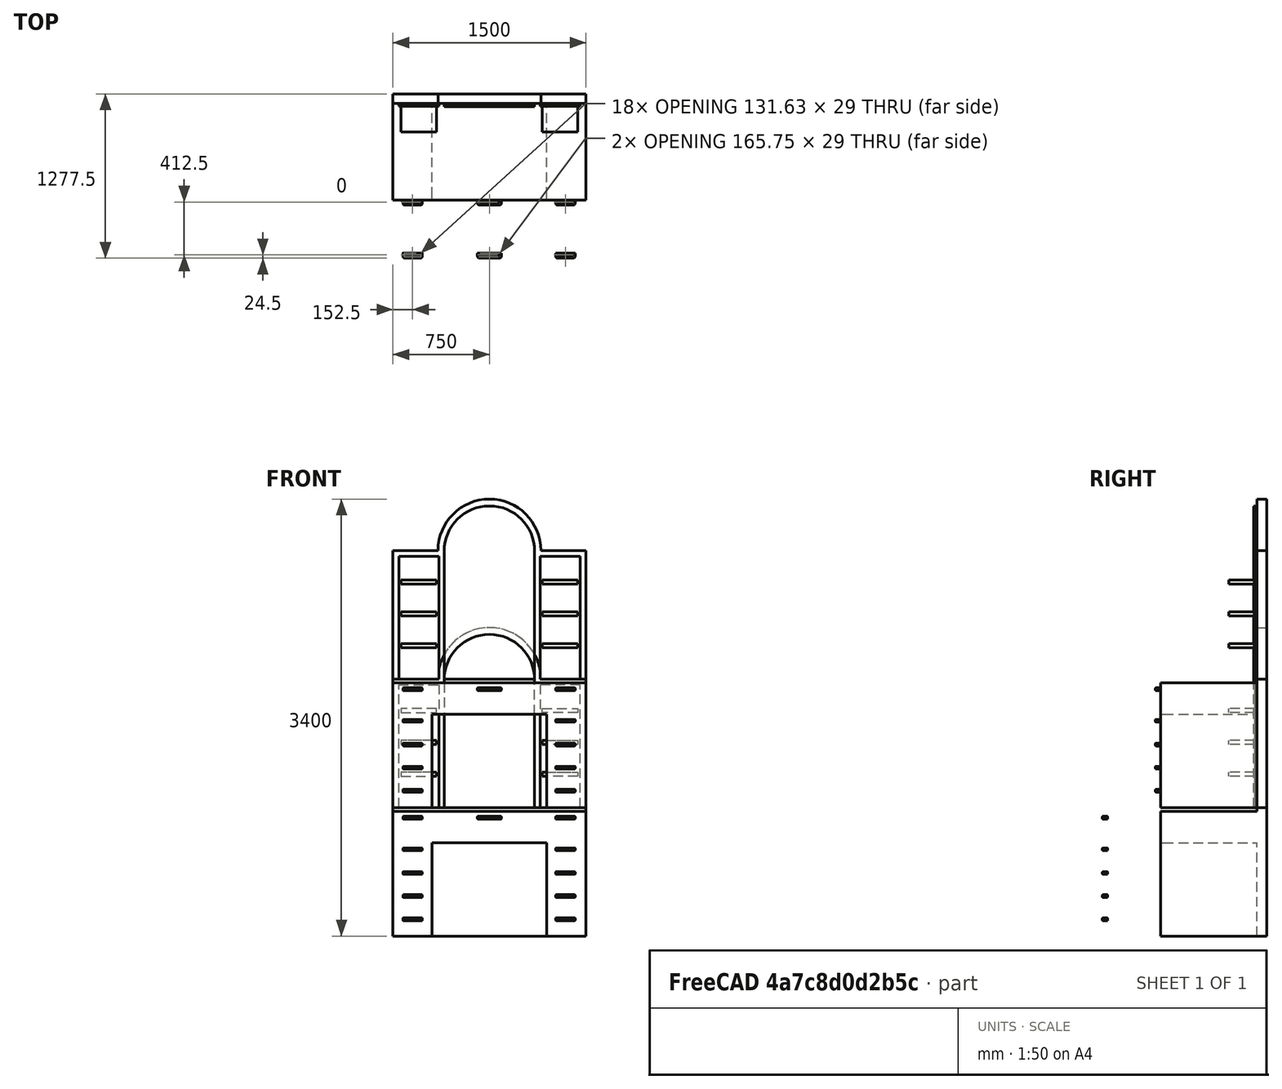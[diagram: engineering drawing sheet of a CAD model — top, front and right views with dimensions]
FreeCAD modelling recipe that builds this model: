
FCSTD DOCUMENT  (FreeCAD 1.0R39109 (Git))
Label: DressingTable
License: All rights reserved
LicenseURL: https://en.wikipedia.org/wiki/All_rights_reserved
objects: Sketcher::SketchObject×30, PartDesign::Fillet×22, PartDesign::Pad×18, PartDesign::Body×13, PartDesign::Pocket×12, PartDesign::ShapeBinder×12, PartDesign::Plane×12, Assembly::JointGroup×3, App::Link×3, Assembly::AssemblyObject×3, Part::FeaturePython×3, App::Part×2
note: 256 computed .brp shape members not serialized (recipe doc carries the construction recipe); baked Part::Feature solids carry a one-line shape summary decoded from their .brp

FEATURE [Sketcher::SketchObject] Sketch
  ArcFitTolerance = 1e-06
  AttachmentSupport = -> [XZ_Plane]
  FullyConstrained = true
  MakeInternals = false
  MapMode = 5
  Placement = pos=(0,0,0) rot=(1,0,0;1.5708rad)
  sketch-geometry (7):
    g0: LineSegment StartX=-750 StartY=-1000 StartZ=0 EndX=750 EndY=-1000 EndZ=0
    g1: LineSegment StartX=750 StartY=-1000 StartZ=0 EndX=750 EndY=1000 EndZ=0
    g2: LineSegment StartX=750 StartY=1000 StartZ=0 EndX=400 EndY=1000 EndZ=0
    g3: LineSegment StartX=-750 StartY=1000 StartZ=0 EndX=-750 EndY=-1000 EndZ=0
    g4: GeomPoint [constr] X=0 Y=0 Z=0
    g5: ArcOfCircle CenterX=1.35e-14 CenterY=1000 CenterZ=0 NormalX=0 NormalY=0 NormalZ=1 AngleXU=0 Radius=400 StartAngle=0 EndAngle=3.14159
    g6: LineSegment StartX=-400 StartY=1000 StartZ=0 EndX=-750 EndY=1000 EndZ=0
  constraints (18):
    c: Coincident(g0,g1)
    c: Coincident(g1,g2)
    c: Coincident(g6,g3)
    c: Coincident(g3,g0)
    c: Horizontal(g0)
    c: Horizontal(g2)
    c: Vertical(g1)
    c: Vertical(g3)
    c: Symmetric(g2,g0,g4)
    c: Coincident(g4,g-1)
    c: DistanceY(g1,g1) = 2000
    c: DistanceX(g6,g2) = 1500
    c: Symmetric(g1,g6,g5)
    c: Diameter(g5) = 800
    c: Coincident(g5,g6)
    c: Coincident(g5,g2)
    c: Horizontal(g6)
    c: Horizontal(g5,g2)
FEATURE [PartDesign::Pad] Pad
  Direction = (0,-1,2e-16)
  Length = 75
  Length2 = 10
  Placement = pos=(0,0,0) rot=(1,0,0;1.5708rad)
  Profile = -> Sketch
  ReferenceAxis = -> Sketch [N_Axis]
  Refine = true
  Suppressed = false
  Type = 0
FEATURE [Sketcher::SketchObject] Sketch001
  ArcFitTolerance = 1e-06
  AttachmentSupport = -> [Pad]
  FullyConstrained = false
  MakeInternals = false
  MapMode = 5
  Placement = pos=(0,-75,0) rot=(1,0,0;1.5708rad)
  sketch-geometry (14):
    g0: LineSegment [constr] StartX=0 StartY=0 StartZ=0 EndX=936.468 EndY=0 EndZ=0
    g1: LineSegment [constr] StartX=0 StartY=0 StartZ=0 EndX=-879.559 EndY=0 EndZ=0
    g2: ArcOfCircle CenterX=0 CenterY=995.137 CenterZ=0 NormalX=0 NormalY=0 NormalZ=1 AngleXU=0 Radius=351.618 StartAngle=0 EndAngle=3.14159
    g3: LineSegment StartX=-351.618 StartY=995.137 StartZ=0 EndX=-351.618 EndY=0 EndZ=0
    g4: LineSegment StartX=351.618 StartY=995.137 StartZ=0 EndX=351.618 EndY=0 EndZ=0
    g5: LineSegment StartX=-351.618 StartY=0 StartZ=0 EndX=351.618 EndY=0 EndZ=0
    g6: LineSegment StartX=393.332 StartY=955.725 StartZ=0 EndX=393.332 EndY=0 EndZ=0
    g7: LineSegment StartX=393.332 StartY=0 StartZ=0 EndX=704.851 EndY=0 EndZ=0
    g8: LineSegment StartX=704.851 StartY=0 StartZ=0 EndX=704.851 EndY=955.725 EndZ=0
    g9: LineSegment StartX=704.851 StartY=955.725 StartZ=0 EndX=393.332 EndY=955.725 EndZ=0
    g10: LineSegment StartX=-393.332 StartY=955.725 StartZ=0 EndX=-393.332 EndY=0 EndZ=0
    g11: LineSegment StartX=-393.332 StartY=0 StartZ=0 EndX=-704.851 EndY=0 EndZ=0
    g12: LineSegment StartX=-704.851 StartY=0 StartZ=0 EndX=-704.851 EndY=955.725 EndZ=0
    g13: LineSegment StartX=-704.851 StartY=955.725 StartZ=0 EndX=-393.332 EndY=955.725 EndZ=0
  constraints (30):
    c: Coincident(g0,g-1)
    c: Horizontal(g0)
    c: Coincident(g1,g0)
    c: PointOnObject(g1,g-1)
    c: PointOnObject(g2,g-2)
    c: PointOnObject(g3,g1)
    c: Vertical(g3)
    c: PointOnObject(g4,g0)
    c: Vertical(g4)
    c: Tangent(g4,g2) = 1.5708
    c: Tangent(g3,g2) = -1.5708
    c: Coincident(g5,g3)
    c: Coincident(g5,g4)
    c: Coincident(g6,g7)
    c: Coincident(g7,g8)
    c: Coincident(g8,g9)
    c: Coincident(g9,g6)
    c: Vertical(g6)
    c: Vertical(g8)
    c: Horizontal(g7)
    c: Horizontal(g9)
    c: PointOnObject(g7,g0)
    c: Coincident(g10,g11)
    c: Coincident(g11,g12)
    c: Coincident(g12,g13)
    c: Coincident(g13,g10)
    c: Vertical(g10)
    c: Vertical(g12)
    c: Horizontal(g11)
    c: Horizontal(g13)
FEATURE [PartDesign::Pad] Pad001
  BaseFeature = -> Pad
  Direction = (0,-1,2e-16)
  Length = 20
  Length2 = 10
  Placement = pos=(0,0,0) rot=(1,0,0;1.5708rad)
  Profile = -> Sketch001
  ReferenceAxis = -> Sketch001 [N_Axis]
  Refine = true
  Suppressed = false
  Type = 0
FEATURE [Sketcher::SketchObject] Sketch002
  ArcFitTolerance = 1e-06
  AttachmentSupport = -> [Pad001]
  ExternalGeometry = -> [Pad001]
  FullyConstrained = false
  MakeInternals = false
  MapMode = 5
  Placement = pos=(0,-95,2.09e-14) rot=(1,0,0;1.5708rad)
  sketch-geometry (27):
    g0: LineSegment StartX=-686.592 StartY=770.22 StartZ=0 EndX=-686.592 EndY=738.354 EndZ=0
    g1: LineSegment StartX=-686.592 StartY=738.354 StartZ=0 EndX=-411.592 EndY=738.354 EndZ=0
    g2: LineSegment StartX=-411.592 StartY=738.354 StartZ=0 EndX=-411.592 EndY=770.22 EndZ=0
    g3: LineSegment StartX=-411.592 StartY=770.22 StartZ=0 EndX=-686.592 EndY=770.22 EndZ=0
    g4: LineSegment StartX=-686.592 StartY=523.301 StartZ=0 EndX=-686.592 EndY=491.435 EndZ=0
    g5: LineSegment StartX=-686.592 StartY=491.435 StartZ=0 EndX=-411.592 EndY=491.435 EndZ=0
    g6: LineSegment StartX=-411.592 StartY=491.435 StartZ=0 EndX=-411.592 EndY=523.301 EndZ=0
    g7: LineSegment StartX=-411.592 StartY=523.301 StartZ=0 EndX=-686.592 EndY=523.301 EndZ=0
    g8: LineSegment StartX=-686.592 StartY=276.382 StartZ=0 EndX=-686.592 EndY=244.516 EndZ=0
    g9: LineSegment StartX=-686.592 StartY=244.516 StartZ=0 EndX=-411.592 EndY=244.516 EndZ=0
    g10: LineSegment StartX=-411.592 StartY=244.516 StartZ=0 EndX=-411.592 EndY=276.382 EndZ=0
    g11: LineSegment StartX=-411.592 StartY=276.382 StartZ=0 EndX=-686.592 EndY=276.382 EndZ=0
    g12: LineSegment [constr] StartX=-686.592 StartY=738.354 StartZ=0 EndX=-686.592 EndY=523.301 EndZ=0
    g13: LineSegment [constr] StartX=-686.592 StartY=491.435 StartZ=0 EndX=-686.592 EndY=276.382 EndZ=0
    g14: LineSegment [constr] StartX=-549.092 StartY=477.863 StartZ=0 EndX=-549.092 EndY=955.725 EndZ=0
    g15: LineSegment StartX=686.592 StartY=738.354 StartZ=0 EndX=411.592 EndY=738.354 EndZ=0
    g16: LineSegment StartX=411.592 StartY=770.22 StartZ=0 EndX=686.592 EndY=770.22 EndZ=0
    g17: LineSegment StartX=411.592 StartY=738.354 StartZ=0 EndX=411.592 EndY=770.22 EndZ=0
    g18: LineSegment StartX=686.592 StartY=770.22 StartZ=0 EndX=686.592 EndY=738.354 EndZ=0
    g19: LineSegment StartX=411.592 StartY=523.301 StartZ=0 EndX=686.592 EndY=523.301 EndZ=0
    g20: LineSegment StartX=411.592 StartY=491.435 StartZ=0 EndX=411.592 EndY=523.301 EndZ=0
    g21: LineSegment StartX=686.592 StartY=491.435 StartZ=0 EndX=411.592 EndY=491.435 EndZ=0
    g22: LineSegment StartX=686.592 StartY=523.301 StartZ=0 EndX=686.592 EndY=491.435 EndZ=0
    g23: LineSegment StartX=411.592 StartY=244.516 StartZ=0 EndX=411.592 EndY=276.382 EndZ=0
    g24: LineSegment StartX=686.592 StartY=244.516 StartZ=0 EndX=411.592 EndY=244.516 EndZ=0
    g25: LineSegment StartX=411.592 StartY=276.382 StartZ=0 EndX=686.592 EndY=276.382 EndZ=0
    g26: LineSegment StartX=686.592 StartY=276.382 StartZ=0 EndX=686.592 EndY=244.516 EndZ=0
  constraints (66):
    c: Coincident(g0,g1)
    c: Coincident(g1,g2)
    c: Coincident(g2,g3)
    c: Coincident(g3,g0)
    c: Vertical(g0)
    c: Vertical(g2)
    c: Horizontal(g1)
    c: Horizontal(g3)
    c: Coincident(g4,g5)
    c: Coincident(g5,g6)
    c: Coincident(g6,g7)
    c: Coincident(g7,g4)
    c: Vertical(g4)
    c: Vertical(g6)
    c: Horizontal(g5)
    c: Horizontal(g7)
    c: Coincident(g8,g9)
    c: Coincident(g9,g10)
    c: Coincident(g10,g11)
    c: Coincident(g11,g8)
    c: Vertical(g8)
    c: Vertical(g10)
    c: Horizontal(g9)
    c: Horizontal(g11)
    c: Coincident(g12,g0)
    c: Coincident(g12,g4)
    c: Vertical(g12)
    c: Coincident(g13,g4)
    c: Coincident(g13,g8)
    c: Vertical(g13)
    c: Equal(g12,g13)
    c: Equal(g2,g6)
    c: Equal(g6,g10)
    c: Equal(g11,g7)
    c: Equal(g7,g3)
    c: DistanceX(g3,g3) = 275
    c: Symmetric(g2,g0,g14)
    c: Symmetric(g-5,g-5,g14)
    c: Coincident(g18,g15)
    c: Coincident(g15,g17)
    c: Coincident(g17,g16)
    c: Coincident(g16,g18)
    c: Vertical(g18)
    c: Vertical(g17)
    c: Horizontal(g15)
    c: Horizontal(g16)
    c: Coincident(g22,g21)
    c: Coincident(g21,g20)
    c: Coincident(g20,g19)
    c: Coincident(g19,g22)
    c: Vertical(g22)
    c: Vertical(g20)
    c: Horizontal(g21)
    c: Horizontal(g19)
    c: Coincident(g26,g24)
    c: Coincident(g24,g23)
    c: Coincident(g23,g25)
    c: Coincident(g25,g26)
    c: Vertical(g26)
    c: Vertical(g23)
    c: Horizontal(g24)
    c: Horizontal(g25)
    c: Equal(g17,g20)
    c: Equal(g20,g23)
    c: Equal(g25,g19)
    c: Equal(g19,g16)
FEATURE [PartDesign::Pad] Pad002
  BaseFeature = -> Pad001
  Direction = (0,-1,2e-16)
  Length = 200
  Length2 = 10
  Placement = pos=(0,0,0) rot=(1,0,0;1.5708rad)
  Profile = -> Sketch002
  ReferenceAxis = -> Sketch002 [N_Axis]
  Refine = true
  Suppressed = false
  Type = 0
FEATURE [Sketcher::SketchObject] Sketch003
  ArcFitTolerance = 1e-06
  AttachmentSupport = -> [Pad002]
  ExternalGeometry = -> [Pad002]
  FullyConstrained = true
  MakeInternals = false
  MapMode = 5
  Placement = pos=(0,-75,0) rot=(1,0,0;1.5708rad)
  sketch-geometry (4):
    g0: LineSegment StartX=-750 StartY=-1000 StartZ=0 EndX=750 EndY=-1000 EndZ=0
    g1: LineSegment StartX=750 StartY=-1000 StartZ=0 EndX=750 EndY=-30 EndZ=0
    g2: LineSegment StartX=750 StartY=-30 StartZ=0 EndX=-750 EndY=-30 EndZ=0
    g3: LineSegment StartX=-750 StartY=-30 StartZ=0 EndX=-750 EndY=-1000 EndZ=0
  constraints (11):
    c: Coincident(g0,g1)
    c: Coincident(g1,g2)
    c: Coincident(g2,g3)
    c: Coincident(g3,g0)
    c: Horizontal(g0)
    c: Horizontal(g2)
    c: Vertical(g1)
    c: Vertical(g3)
    c: Coincident(g0,g-3)
    c: PointOnObject(g1,g-4)
    c: DistanceY(g1,g1) = 970
FEATURE [PartDesign::Pad] Pad003
  BaseFeature = -> Pad002
  Direction = (0,-1,2e-16)
  Length = 750
  Length2 = 10
  Placement = pos=(0,0,0) rot=(1,0,0;1.5708rad)
  Profile = -> Sketch003
  ReferenceAxis = -> Sketch003 [N_Axis]
  Suppressed = false
  Type = 0
FEATURE [Sketcher::SketchObject] Sketch004
  ArcFitTolerance = 1e-06
  AttachmentSupport = -> [Pad003]
  ExternalGeometry = -> [Pad003]
  FullyConstrained = true
  MakeInternals = false
  MapMode = 5
  Placement = pos=(0,-825,1.897e-13) rot=(1,0,0;1.5708rad)
  sketch-geometry (4):
    g0: LineSegment StartX=-445 StartY=-1000 StartZ=0 EndX=445 EndY=-1000 EndZ=0
    g1: LineSegment StartX=445 StartY=-1000 StartZ=0 EndX=445 EndY=-275 EndZ=0
    g2: LineSegment StartX=445 StartY=-275 StartZ=0 EndX=-445 EndY=-275 EndZ=0
    g3: LineSegment StartX=-445 StartY=-275 StartZ=0 EndX=-445 EndY=-1000 EndZ=0
  constraints (11):
    c: Coincident(g0,g1)
    c: Coincident(g1,g2)
    c: Coincident(g2,g3)
    c: Coincident(g3,g0)
    c: Horizontal(g0)
    c: Vertical(g1)
    c: Vertical(g3)
    c: PointOnObject(g0,g-3)
    c: DistanceX(g2,g2) = 890
    c: DistanceY(g1,g1) = 725
    c: Symmetric(g1,g2,g-2)
FEATURE [PartDesign::Pocket] Pocket
  BaseFeature = -> Pad003
  Direction = (0,1,-2e-16)
  Length = 750
  Length2 = 5
  Placement = pos=(0,0,0) rot=(1,0,0;1.5708rad)
  Profile = -> Sketch004
  ReferenceAxis = -> Sketch004 [N_Axis]
  Suppressed = false
  Type = 0
FEATURE [Sketcher::SketchObject] Sketch005
  ArcFitTolerance = 1e-06
  AttachmentSupport = -> [Pocket]
  ExternalGeometry = -> [Pocket]
  FullyConstrained = true
  MakeInternals = false
  MapMode = 5
  Placement = pos=(0,-825,1.897e-13) rot=(1,0,0;1.5708rad)
  sketch-geometry (24):
    g0: LineSegment StartX=-445 StartY=-275 StartZ=0 EndX=-445 EndY=-30 EndZ=0
    g1: LineSegment StartX=-445 StartY=-30 StartZ=0 EndX=-750 EndY=-30 EndZ=0
    g2: LineSegment StartX=-750 StartY=-30 StartZ=0 EndX=-750 EndY=-275 EndZ=0
    g3: LineSegment StartX=-750 StartY=-275 StartZ=0 EndX=-445 EndY=-275 EndZ=0
    g4: LineSegment StartX=-445 StartY=-460 StartZ=0 EndX=-750 EndY=-460 EndZ=0
    g5: LineSegment StartX=-750 StartY=-460 StartZ=0 EndX=-750 EndY=-640 EndZ=0
    g6: LineSegment StartX=-750 StartY=-640 StartZ=0 EndX=-445 EndY=-640 EndZ=0
    g7: LineSegment StartX=-445 StartY=-640 StartZ=0 EndX=-445 EndY=-460 EndZ=0
    g8: LineSegment StartX=-750 StartY=-820 StartZ=0 EndX=-445 EndY=-820 EndZ=0
    g9: LineSegment StartX=-750 StartY=-820 StartZ=0 EndX=-750 EndY=-1000 EndZ=0
    g10: LineSegment StartX=-750 StartY=-1000 StartZ=0 EndX=-445 EndY=-1000 EndZ=0
    g11: LineSegment StartX=-445 StartY=-1000 StartZ=0 EndX=-445 EndY=-820 EndZ=0
    g12: LineSegment StartX=750 StartY=-30 StartZ=0 EndX=750 EndY=-275 EndZ=0
    g13: LineSegment StartX=445 StartY=-30 StartZ=0 EndX=750 EndY=-30 EndZ=0
    g14: LineSegment StartX=750 StartY=-275 StartZ=0 EndX=445 EndY=-275 EndZ=0
    g15: LineSegment StartX=445 StartY=-460 StartZ=0 EndX=750 EndY=-460 EndZ=0
    g16: LineSegment StartX=750 StartY=-460 StartZ=0 EndX=750 EndY=-640 EndZ=0
    g17: LineSegment StartX=750 StartY=-640 StartZ=0 EndX=445 EndY=-640 EndZ=0
    g18: LineSegment StartX=445 StartY=-640 StartZ=0 EndX=445 EndY=-460 EndZ=0
    g19: LineSegment StartX=445 StartY=-1000 StartZ=0 EndX=445 EndY=-820 EndZ=0
    g20: LineSegment StartX=750 StartY=-1000 StartZ=0 EndX=445 EndY=-1000 EndZ=0
    g21: LineSegment StartX=750 StartY=-820 StartZ=0 EndX=750 EndY=-1000 EndZ=0
    g22: LineSegment StartX=750 StartY=-820 StartZ=0 EndX=445 EndY=-820 EndZ=0
    g23: LineSegment StartX=445 StartY=-30 StartZ=0 EndX=445 EndY=-275 EndZ=0
  constraints (67):
    c: Coincident(g0,g1)
    c: Vertical(g0)
    c: Horizontal(g1)
    c: Coincident(g0,g-6)
    c: Coincident(g1,g2)
    c: PointOnObject(g2,g-5)
    c: Coincident(g2,g3)
    c: Coincident(g3,g0)
    c: Horizontal(g3)
    c: PointOnObject(g4,g-6)
    c: PointOnObject(g4,g-5)
    c: Horizontal(g4)
    c: Coincident(g4,g5)
    c: PointOnObject(g5,g-5)
    c: Coincident(g5,g6)
    c: PointOnObject(g6,g-6)
    c: Horizontal(g6)
    c: Coincident(g6,g7)
    c: PointOnObject(g8,g-5)
    c: PointOnObject(g8,g-6)
    c: Horizontal(g8)
    c: Coincident(g9,g10)
    c: PointOnObject(g10,g-6)
    c: Horizontal(g10)
    c: Coincident(g10,g11)
    c: Coincident(g11,g8)
    c: Coincident(g9,g-5)
    c: DistanceY(g9,g9) = 180
    c: Coincident(g1,g-5)
    c: Horizontal(g13)
    c: Coincident(g13,g12)
    c: Coincident(g12,g14)
    c: Horizontal(g14)
    c: Horizontal(g15)
    c: Coincident(g15,g16)
    c: Coincident(g16,g17)
    c: Horizontal(g17)
    c: Coincident(g17,g18)
    c: Horizontal(g22)
    c: Coincident(g21,g20)
    c: Horizontal(g20)
    c: Coincident(g20,g19)
    c: Coincident(g19,g22)
    c: Coincident(g12,g-4)
    c: Equal(g14,g13)
    c: Horizontal(g15,g4)
    c: Horizontal(g17,g6)
    c: Horizontal(g22,g8)
    c: Horizontal(g19,g10)
    c: Vertical(g15,g17)
    c: Vertical(g17,g22)
    c: Vertical(g22,g19)
    c: Vertical(g19,g14)
    c: Vertical(g21,g20)
    c: Vertical(g20,g12)
    c: Coincident(g23,g13)
    c: Coincident(g23,g14)
    c: Vertical(g23)
    c: Coincident(g14,g-3)
    c: Coincident(g7,g4)
    c: Equal(g5,g9)
    c: Coincident(g18,g15)
    c: Vertical(g15,g12)
    c: Coincident(g22,g21)
    c: Coincident(g9,g8)
    c: DistanceY(g8,g5) = 180
    c: Vertical(g16,g21)
FEATURE [PartDesign::Pad] Pad004
  BaseFeature = -> Pocket
  Direction = (0,-1,2e-16)
  Length = 25
  Length2 = 10
  Placement = pos=(0,0,0) rot=(1,0,0;1.5708rad)
  Profile = -> Sketch005
  ReferenceAxis = -> Sketch005 [N_Axis]
  Reversed = true
  Suppressed = false
  Type = 0
FEATURE [Sketcher::SketchObject] Sketch006
  ArcFitTolerance = 1e-06
  AttachmentSupport = -> [Pad004]
  ExternalGeometry = -> [Pad004]
  FullyConstrained = true
  MakeInternals = false
  MapMode = 5
  Placement = pos=(0,-825,1.897e-13) rot=(1,0,0;1.5708rad)
  sketch-geometry (20):
    g0: LineSegment StartX=-750 StartY=-275 StartZ=0 EndX=-750 EndY=-460 EndZ=0
    g1: LineSegment StartX=-750 StartY=-460 StartZ=0 EndX=-445 EndY=-460 EndZ=0
    g2: LineSegment StartX=-445 StartY=-460 StartZ=0 EndX=-445 EndY=-275 EndZ=0
    g3: LineSegment StartX=-445 StartY=-275 StartZ=0 EndX=-750 EndY=-275 EndZ=0
    g4: LineSegment StartX=-750 StartY=-640 StartZ=0 EndX=-750 EndY=-820 EndZ=0
    g5: LineSegment StartX=-750 StartY=-820 StartZ=0 EndX=-445 EndY=-820 EndZ=0
    g6: LineSegment StartX=-445 StartY=-820 StartZ=0 EndX=-445 EndY=-640 EndZ=0
    g7: LineSegment StartX=-445 StartY=-640 StartZ=0 EndX=-750 EndY=-640 EndZ=0
    g8: LineSegment StartX=445 StartY=-275 StartZ=0 EndX=445 EndY=-460 EndZ=0
    g9: LineSegment StartX=445 StartY=-460 StartZ=0 EndX=750 EndY=-460 EndZ=0
    g10: LineSegment StartX=750 StartY=-460 StartZ=0 EndX=750 EndY=-275 EndZ=0
    g11: LineSegment StartX=750 StartY=-275 StartZ=0 EndX=445 EndY=-275 EndZ=0
    g12: LineSegment StartX=445 StartY=-640 StartZ=0 EndX=445 EndY=-820 EndZ=0
    g13: LineSegment StartX=445 StartY=-820 StartZ=0 EndX=750 EndY=-820 EndZ=0
    g14: LineSegment StartX=750 StartY=-820 StartZ=0 EndX=750 EndY=-640 EndZ=0
    g15: LineSegment StartX=750 StartY=-640 StartZ=0 EndX=445 EndY=-640 EndZ=0
    g16: LineSegment StartX=-445 StartY=-30 StartZ=0 EndX=-445 EndY=-275 EndZ=0
    g17: LineSegment StartX=-445 StartY=-275 StartZ=0 EndX=445 EndY=-275 EndZ=0
    g18: LineSegment StartX=445 StartY=-275 StartZ=0 EndX=445 EndY=-30 EndZ=0
    g19: LineSegment StartX=445 StartY=-30 StartZ=0 EndX=-445 EndY=-30 EndZ=0
  constraints (50):
    c: Coincident(g0,g1)
    c: Coincident(g1,g2)
    c: Coincident(g2,g3)
    c: Coincident(g3,g0)
    c: Vertical(g0)
    c: Vertical(g2)
    c: Horizontal(g1)
    c: Horizontal(g3)
    c: Coincident(g0,g-4)
    c: Coincident(g1,g-3)
    c: Coincident(g4,g5)
    c: Coincident(g5,g6)
    c: Coincident(g6,g7)
    c: Coincident(g7,g4)
    c: Vertical(g4)
    c: Vertical(g6)
    c: Horizontal(g5)
    c: Horizontal(g7)
    c: Coincident(g4,g-6)
    c: Coincident(g5,g-5)
    c: Coincident(g8,g9)
    c: Coincident(g9,g10)
    c: Coincident(g10,g11)
    c: Coincident(g11,g8)
    c: Vertical(g8)
    c: Vertical(g10)
    c: Horizontal(g9)
    c: Horizontal(g11)
    c: Coincident(g8,g-8)
    c: Coincident(g9,g-9)
    c: Coincident(g12,g13)
    c: Coincident(g13,g14)
    c: Coincident(g14,g15)
    c: Coincident(g15,g12)
    c: Vertical(g12)
    c: Vertical(g14)
    c: Horizontal(g13)
    c: Horizontal(g15)
    c: Coincident(g12,g-10)
    c: Coincident(g13,g-11)
    c: Coincident(g16,g17)
    c: Coincident(g17,g18)
    c: Coincident(g18,g19)
    c: Coincident(g19,g16)
    c: Vertical(g16)
    c: Vertical(g18)
    c: Horizontal(g17)
    c: Horizontal(g19)
    c: Coincident(g16,g-7)
    c: Coincident(g17,g8)
FEATURE [PartDesign::Pad] Pad005
  BaseFeature = -> Pad004
  Direction = (0,-1,2e-16)
  Length = 25
  Length2 = 10
  Placement = pos=(0,0,0) rot=(1,0,0;1.5708rad)
  Profile = -> Sketch006
  ReferenceAxis = -> Sketch006 [N_Axis]
  Reversed = true
  Suppressed = false
  Type = 0
FEATURE [PartDesign::Body] Body
  AllowCompound = false
  Group = -> [Sketch,Pad,Sketch001,Pad001,Sketch002,Pad002,Sketch003,Pad003,Sketch004,Pocket,Sketch005,Pad004,Sketch006,Pad005]
  Origin = -> Origin
  Placement = pos=(0,412.5,0) rot=(0,0,1;0rad)
  Tip = -> Pad005
FEATURE [Assembly::JointGroup] Joints
FEATURE [App::Link] dressing_table001  label="dressing_table002"
  LinkPlacement = pos=(0,412.5,1000) rot=(0,0,1;0rad)
  LinkedObject = -> Body
  Placement = pos=(0,412.5,1000) rot=(0,0,1;0rad)
FEATURE [Assembly::AssemblyObject] Assembly  label="body_a"
  Group = -> [Joints,dressing_table001]
  Origin = -> Origin003
  Placement = pos=(0,412.5,1000) rot=(0,0,1;0rad)
  Type = Assembly
FEATURE [PartDesign::ShapeBinder] CopyPocket001
  Placement = pos=(0,0,0) rot=(1,0,0;1.5708rad)
  TraceSupport = false
FEATURE [PartDesign::Plane] DatumPlane
  AttachmentSupport = -> [CopyPocket001]
  Length = 214.996
  MapMode = 5
  Placement = pos=(0,-825,3.729e-13) rot=(1,0,0;1.5708rad)
  ResizeMode = 0
  Width = 144.392
FEATURE [Sketcher::SketchObject] Sketch008
  ArcFitTolerance = 1e-06
  AttachmentSupport = -> [CopyPocket001]
  ExternalGeometry = -> [CopyPocket001]
  FullyConstrained = true
  MakeInternals = false
  MapMode = 5
  Placement = pos=(0,-825,3.729e-13) rot=(1,0,0;1.5708rad)
  sketch-geometry (4):
    g0: LineSegment StartX=-92.8734 StartY=-68.8715 StartZ=0 EndX=-92.8734 EndY=-90.1429 EndZ=0
    g1: LineSegment StartX=-92.8734 StartY=-90.1429 StartZ=0 EndX=92.8734 EndY=-90.1429 EndZ=0
    g2: LineSegment StartX=92.8734 StartY=-90.1429 StartZ=0 EndX=92.8734 EndY=-68.8715 EndZ=0
    g3: LineSegment StartX=92.8734 StartY=-68.8715 StartZ=0 EndX=-92.8734 EndY=-68.8715 EndZ=0
  constraints (10):
    c: Coincident(g0,g1)
    c: Coincident(g1,g2)
    c: Coincident(g2,g3)
    c: Coincident(g3,g0)
    c: Vertical(g0)
    c: Vertical(g2)
    c: Horizontal(g1)
    c: Horizontal(g3)
    c: Coincident(g0,g-3)
    c: Coincident(g1,g-5)
FEATURE [PartDesign::Pad] Pad006
  Direction = (0,-1,2e-16)
  Length = 40
  Length2 = 10
  Placement = pos=(0,0,0) rot=(1,0,0;1.5708rad)
  Profile = -> Sketch008
  ReferenceAxis = -> Sketch008 [N_Axis]
  Refine = true
  Suppressed = false
  Type = 0
FEATURE [Sketcher::SketchObject] Sketch009
  ArcFitTolerance = 1e-06
  AttachmentSupport = -> [Pad006]
  ExternalGeometry = -> [Pad006]
  FullyConstrained = true
  MakeInternals = false
  MapMode = 5
  Placement = pos=(0,-2.29e-14,-68.8715) rot=(0,0,1;3.14159rad)
  sketch-geometry (4):
    g0: LineSegment StartX=-77.8734 StartY=850 StartZ=0 EndX=-77.8734 EndY=826 EndZ=0
    g1: LineSegment StartX=77.8734 StartY=850 StartZ=0 EndX=77.8734 EndY=826 EndZ=0
    g2: LineSegment StartX=-77.8734 StartY=850 StartZ=0 EndX=77.8734 EndY=850 EndZ=0
    g3: LineSegment StartX=-77.8734 StartY=826 StartZ=0 EndX=77.8734 EndY=826 EndZ=0
  constraints (12):
    c: Coincident(g2,g0)
    c: Coincident(g2,g1)
    c: Horizontal(g2)
    c: DistanceX(g-3,g0) = 15
    c: DistanceX(g1,g-3) = 15
    c: Vertical(g0)
    c: Vertical(g1)
    c: DistanceY(g0,g-4) = 15
    c: DistanceY(g-3,g0) = 1
    c: DistanceY(g-3,g1) = 1
    c: Coincident(g3,g0)
    c: Coincident(g3,g1)
FEATURE [PartDesign::Pocket] Pocket002
  BaseFeature = -> Pad006
  Direction = (0,0,-1)
  Length = 5
  Length2 = 5
  Placement = pos=(0,0,0) rot=(1,0,0;1.5708rad)
  Profile = -> Sketch009
  ReferenceAxis = -> Sketch009 [N_Axis]
  Refine = true
  Suppressed = false
  Type = 1
FEATURE [PartDesign::Fillet] Fillet
  Base = -> Pocket002 [Edge22,Edge21,Edge4,Edge20]
  BaseFeature = -> Pocket002
  Placement = pos=(0,0,0) rot=(1,0,0;1.5708rad)
  Radius = 15
  Refine = true
  SupportTransform = false
  Suppressed = false
  UseAllEdges = false
FEATURE [PartDesign::Fillet] Fillet001
  Base = -> Fillet [Edge8,Edge20,Edge10,Edge26]
  BaseFeature = -> Fillet
  Placement = pos=(0,0,0) rot=(1,0,0;1.5708rad)
  Radius = 5
  Refine = true
  SupportTransform = false
  Suppressed = false
  UseAllEdges = false
FEATURE [PartDesign::Body] Body001
  AllowCompound = false
  Group = -> [DatumPlane,CopyPocket001,Sketch008,Pad006,Sketch009,Pocket002,Fillet,Fillet001]
  Origin = -> Origin005
  Tip = -> Fillet001
FEATURE [PartDesign::ShapeBinder] CopyPocket002
  Placement = pos=(0,0,0) rot=(1,0,0;1.5708rad)
  TraceSupport = false
FEATURE [PartDesign::Plane] DatumPlane001
  AttachmentSupport = -> [CopyPocket002]
  Length = 755.028
  MapMode = 5
  Placement = pos=(0,-825,3.729e-13) rot=(1,0,0;1.5708rad)
  ResizeMode = 0
  Width = 171.855
FEATURE [Sketcher::SketchObject] Sketch010
  ArcFitTolerance = 1e-06
  AttachmentSupport = -> [CopyPocket002]
  ExternalGeometry = -> [CopyPocket002]
  FullyConstrained = true
  MakeInternals = false
  MapMode = 5
  Placement = pos=(0,-825,3.729e-13) rot=(1,0,0;1.5708rad)
  sketch-geometry (4):
    g0: LineSegment StartX=-673.316 StartY=-90.1429 StartZ=0 EndX=-521.684 EndY=-90.1429 EndZ=0
    g1: LineSegment StartX=-521.684 StartY=-90.1429 StartZ=0 EndX=-521.684 EndY=-68.8715 EndZ=0
    g2: LineSegment StartX=-521.684 StartY=-68.8715 StartZ=0 EndX=-673.316 EndY=-68.8715 EndZ=0
    g3: LineSegment StartX=-673.316 StartY=-68.8715 StartZ=0 EndX=-673.316 EndY=-90.1429 EndZ=0
  constraints (10):
    c: Coincident(g0,g1)
    c: Coincident(g1,g2)
    c: Coincident(g2,g3)
    c: Coincident(g3,g0)
    c: Horizontal(g0)
    c: Horizontal(g2)
    c: Vertical(g1)
    c: Vertical(g3)
    c: Coincident(g0,g-4)
    c: Coincident(g1,g-3)
FEATURE [PartDesign::Pad] Pad007
  Direction = (0,-1,2e-16)
  Length = 40
  Length2 = 10
  Placement = pos=(0,0,0) rot=(1,0,0;1.5708rad)
  Profile = -> Sketch010
  ReferenceAxis = -> Sketch010 [N_Axis]
  Refine = true
  Suppressed = false
  Type = 0
FEATURE [Sketcher::SketchObject] Sketch011
  ArcFitTolerance = 1e-06
  AttachmentSupport = -> [Pad007]
  ExternalGeometry = -> [Pad007]
  FullyConstrained = true
  MakeInternals = false
  MapMode = 5
  Placement = pos=(0,-2.29e-14,-68.8715) rot=(0,0,1;3.14159rad)
  sketch-geometry (4):
    g0: LineSegment StartX=536.684 StartY=850 StartZ=0 EndX=536.684 EndY=826 EndZ=0
    g1: LineSegment StartX=536.684 StartY=826 StartZ=0 EndX=658.316 EndY=826 EndZ=0
    g2: LineSegment StartX=658.316 StartY=826 StartZ=0 EndX=658.316 EndY=850 EndZ=0
    g3: LineSegment StartX=658.316 StartY=850 StartZ=0 EndX=536.684 EndY=850 EndZ=0
  constraints (12):
    c: Coincident(g0,g1)
    c: Coincident(g1,g2)
    c: Coincident(g2,g3)
    c: Coincident(g3,g0)
    c: Vertical(g0)
    c: Vertical(g2)
    c: Horizontal(g1)
    c: Horizontal(g3)
    c: DistanceY(g-4,g1) = 1
    c: DistanceX(g1,g-4) = 15
    c: DistanceY(g2,g-4) = 15
    c: DistanceX(g-3,g0) = 15
FEATURE [PartDesign::Pocket] Pocket003
  BaseFeature = -> Pad007
  Direction = (0,0,-1)
  Length = 5
  Length2 = 5
  Placement = pos=(0,0,0) rot=(1,0,0;1.5708rad)
  Profile = -> Sketch011
  ReferenceAxis = -> Sketch011 [N_Axis]
  Refine = true
  Suppressed = false
  Type = 1
FEATURE [PartDesign::Fillet] Fillet002
  Base = -> Pocket003 [Edge19,Edge14,Edge23,Edge11]
  BaseFeature = -> Pocket003
  Placement = pos=(0,0,0) rot=(1,0,0;1.5708rad)
  Radius = 15
  Refine = true
  SupportTransform = false
  Suppressed = false
  UseAllEdges = false
FEATURE [PartDesign::Fillet] Fillet003
  Base = -> Fillet002 [Edge21,Edge4,Edge32,Edge10]
  BaseFeature = -> Fillet002
  Placement = pos=(0,0,0) rot=(1,0,0;1.5708rad)
  Radius = 5
  Refine = true
  SupportTransform = false
  Suppressed = false
  UseAllEdges = false
FEATURE [PartDesign::Body] Body002
  AllowCompound = false
  Group = -> [DatumPlane001,CopyPocket002,Sketch010,Pad007,Sketch011,Pocket003,Fillet002,Fillet003]
  Origin = -> Origin007
  Tip = -> Fillet003
FEATURE [PartDesign::ShapeBinder] CopyPocket003
  Placement = pos=(0,0,0) rot=(1,0,0;1.5708rad)
  TraceSupport = false
FEATURE [PartDesign::Plane] DatumPlane002
  AttachmentSupport = -> [CopyPocket003]
  Length = 798.615
  MapMode = 5
  Placement = pos=(0,-825,3.729e-13) rot=(1,0,0;1.5708rad)
  ResizeMode = 0
  Width = 460.441
FEATURE [Sketcher::SketchObject] Sketch012
  ArcFitTolerance = 1e-06
  AttachmentSupport = -> [CopyPocket003]
  ExternalGeometry = -> [CopyPocket003]
  FullyConstrained = true
  MakeInternals = false
  MapMode = 5
  Placement = pos=(0,-825,3.729e-13) rot=(1,0,0;1.5708rad)
  sketch-geometry (4):
    g0: LineSegment StartX=-673.316 StartY=-313.872 StartZ=0 EndX=-673.316 EndY=-335.143 EndZ=0
    g1: LineSegment StartX=-673.316 StartY=-335.143 StartZ=0 EndX=-521.684 EndY=-335.143 EndZ=0
    g2: LineSegment StartX=-521.684 StartY=-335.143 StartZ=0 EndX=-521.684 EndY=-313.872 EndZ=0
    g3: LineSegment StartX=-521.684 StartY=-313.872 StartZ=0 EndX=-673.316 EndY=-313.872 EndZ=0
  constraints (10):
    c: Coincident(g0,g1)
    c: Coincident(g1,g2)
    c: Coincident(g2,g3)
    c: Coincident(g3,g0)
    c: Vertical(g0)
    c: Vertical(g2)
    c: Horizontal(g1)
    c: Horizontal(g3)
    c: Coincident(g0,g-4)
    c: Coincident(g1,g-3)
FEATURE [PartDesign::Pad] Pad008
  Direction = (0,-1,2e-16)
  Length = 40
  Length2 = 10
  Placement = pos=(0,0,0) rot=(1,0,0;1.5708rad)
  Profile = -> Sketch012
  ReferenceAxis = -> Sketch012 [N_Axis]
  Refine = true
  Suppressed = false
  Type = 0
FEATURE [Sketcher::SketchObject] Sketch013
  ArcFitTolerance = 1e-06
  AttachmentSupport = -> [Pad008]
  ExternalGeometry = -> [Pad008]
  FullyConstrained = true
  MakeInternals = false
  MapMode = 5
  Placement = pos=(0,-1.045e-13,-313.872) rot=(0,0,1;3.14159rad)
  sketch-geometry (4):
    g0: LineSegment StartX=536.684 StartY=850 StartZ=0 EndX=536.684 EndY=826 EndZ=0
    g1: LineSegment StartX=536.684 StartY=826 StartZ=0 EndX=658.316 EndY=826 EndZ=0
    g2: LineSegment StartX=658.316 StartY=826 StartZ=0 EndX=658.316 EndY=850 EndZ=0
    g3: LineSegment StartX=658.316 StartY=850 StartZ=0 EndX=536.684 EndY=850 EndZ=0
  constraints (12):
    c: Coincident(g0,g1)
    c: Coincident(g1,g2)
    c: Coincident(g2,g3)
    c: Coincident(g3,g0)
    c: Vertical(g0)
    c: Vertical(g2)
    c: Horizontal(g1)
    c: Horizontal(g3)
    c: DistanceY(g-4,g1) = 1
    c: DistanceX(g1,g-4) = 15
    c: DistanceY(g0,g-3) = 15
    c: DistanceX(g-3,g0) = 15
FEATURE [PartDesign::Pocket] Pocket004
  BaseFeature = -> Pad008
  Direction = (0,0,-1)
  Length = 5
  Length2 = 5
  Placement = pos=(0,0,0) rot=(1,0,0;1.5708rad)
  Profile = -> Sketch013
  ReferenceAxis = -> Sketch013 [N_Axis]
  Refine = true
  Suppressed = false
  Type = 1
FEATURE [PartDesign::Fillet] Fillet004
  Base = -> Pocket004 [Edge20,Edge4,Edge21,Edge22]
  BaseFeature = -> Pocket004
  Placement = pos=(0,0,0) rot=(1,0,0;1.5708rad)
  Radius = 15
  Refine = true
  SupportTransform = false
  Suppressed = false
  UseAllEdges = false
FEATURE [PartDesign::Fillet] Fillet005
  Base = -> Fillet004 [Edge8,Edge20,Edge10,Edge26]
  BaseFeature = -> Fillet004
  Placement = pos=(0,0,0) rot=(1,0,0;1.5708rad)
  Radius = 5
  Refine = true
  SupportTransform = false
  Suppressed = false
  UseAllEdges = false
FEATURE [PartDesign::Body] Body003
  AllowCompound = false
  Group = -> [DatumPlane002,CopyPocket003,Sketch012,Pad008,Sketch013,Pocket004,Fillet004,Fillet005]
  Origin = -> Origin008
  Tip = -> Fillet005
FEATURE [PartDesign::ShapeBinder] CopyPocket004
  Placement = pos=(0,0,0) rot=(1,0,0;1.5708rad)
  TraceSupport = false
FEATURE [PartDesign::Plane] DatumPlane003
  AttachmentSupport = -> [CopyPocket004]
  Length = 821.715
  MapMode = 5
  Placement = pos=(0,-825,3.729e-13) rot=(1,0,0;1.5708rad)
  ResizeMode = 0
  Width = 668.542
FEATURE [Sketcher::SketchObject] Sketch014
  ArcFitTolerance = 1e-06
  AttachmentSupport = -> [CopyPocket004]
  ExternalGeometry = -> [CopyPocket004]
  FullyConstrained = true
  MakeInternals = false
  MapMode = 5
  Placement = pos=(0,-825,3.729e-13) rot=(1,0,0;1.5708rad)
  sketch-geometry (4):
    g0: LineSegment StartX=-673.316 StartY=-498.872 StartZ=0 EndX=-673.316 EndY=-520.143 EndZ=0
    g1: LineSegment StartX=-673.316 StartY=-520.143 StartZ=0 EndX=-521.684 EndY=-520.143 EndZ=0
    g2: LineSegment StartX=-521.684 StartY=-520.143 StartZ=0 EndX=-521.684 EndY=-498.872 EndZ=0
    g3: LineSegment StartX=-521.684 StartY=-498.872 StartZ=0 EndX=-673.316 EndY=-498.872 EndZ=0
  constraints (10):
    c: Coincident(g0,g1)
    c: Coincident(g1,g2)
    c: Coincident(g2,g3)
    c: Coincident(g3,g0)
    c: Vertical(g0)
    c: Vertical(g2)
    c: Horizontal(g1)
    c: Horizontal(g3)
    c: Coincident(g0,g-3)
    c: Coincident(g1,g-4)
FEATURE [PartDesign::Pad] Pad009
  Direction = (0,-1,2e-16)
  Length = 40
  Length2 = 10
  Placement = pos=(0,0,0) rot=(1,0,0;1.5708rad)
  Profile = -> Sketch014
  ReferenceAxis = -> Sketch014 [N_Axis]
  Refine = true
  Suppressed = false
  Type = 0
FEATURE [Sketcher::SketchObject] Sketch015
  ArcFitTolerance = 1e-06
  AttachmentSupport = -> [Pad009]
  ExternalGeometry = -> [Pad009]
  FullyConstrained = true
  MakeInternals = false
  MapMode = 5
  Placement = pos=(0,-1.662e-13,-498.872) rot=(0,0,1;3.14159rad)
  sketch-geometry (4):
    g0: LineSegment StartX=536.684 StartY=850 StartZ=0 EndX=536.684 EndY=826 EndZ=0
    g1: LineSegment StartX=536.684 StartY=826 StartZ=0 EndX=658.316 EndY=826 EndZ=0
    g2: LineSegment StartX=658.316 StartY=826 StartZ=0 EndX=658.316 EndY=850 EndZ=0
    g3: LineSegment StartX=658.316 StartY=850 StartZ=0 EndX=536.684 EndY=850 EndZ=0
  constraints (12):
    c: Coincident(g0,g1)
    c: Coincident(g1,g2)
    c: Coincident(g2,g3)
    c: Coincident(g3,g0)
    c: Vertical(g0)
    c: Vertical(g2)
    c: Horizontal(g1)
    c: Horizontal(g3)
    c: DistanceX(g1,g-4) = 15
    c: DistanceY(g-4,g1) = 1
    c: DistanceY(g0,g-3) = 15
    c: DistanceX(g-3,g0) = 15
FEATURE [PartDesign::Pocket] Pocket005
  BaseFeature = -> Pad009
  Direction = (0,0,-1)
  Length = 5
  Length2 = 5
  Placement = pos=(0,0,0) rot=(1,0,0;1.5708rad)
  Profile = -> Sketch015
  ReferenceAxis = -> Sketch015 [N_Axis]
  Refine = true
  Suppressed = false
  Type = 1
FEATURE [PartDesign::Fillet] Fillet006
  Base = -> Pocket005 [Edge22,Edge21,Edge4,Edge20]
  BaseFeature = -> Pocket005
  Placement = pos=(0,0,0) rot=(1,0,0;1.5708rad)
  Radius = 15
  Refine = true
  SupportTransform = false
  Suppressed = false
  UseAllEdges = false
FEATURE [PartDesign::Fillet] Fillet007
  Base = -> Fillet006 [Edge10,Edge1,Edge20,Edge4]
  BaseFeature = -> Fillet006
  Placement = pos=(0,0,0) rot=(1,0,0;1.5708rad)
  Radius = 5
  Refine = true
  SupportTransform = false
  Suppressed = false
  UseAllEdges = false
FEATURE [PartDesign::Body] Body004
  AllowCompound = false
  Group = -> [DatumPlane003,CopyPocket004,Sketch014,Pad009,Sketch015,Pocket005,Fillet006,Fillet007]
  Origin = -> Origin009
  Tip = -> Fillet007
FEATURE [PartDesign::ShapeBinder] CopyPocket005
  Placement = pos=(0,0,0) rot=(1,0,0;1.5708rad)
  TraceSupport = false
FEATURE [PartDesign::Plane] DatumPlane004
  AttachmentSupport = -> [CopyPocket005]
  Length = 840.637
  MapMode = 5
  Placement = pos=(0,-825,3.729e-13) rot=(1,0,0;1.5708rad)
  ResizeMode = 0
  Width = 867.464
FEATURE [Sketcher::SketchObject] Sketch016
  ArcFitTolerance = 1e-06
  AttachmentSupport = -> [CopyPocket005]
  ExternalGeometry = -> [CopyPocket005]
  FullyConstrained = true
  MakeInternals = false
  MapMode = 5
  Placement = pos=(0,-825,3.729e-13) rot=(1,0,0;1.5708rad)
  sketch-geometry (4):
    g0: LineSegment StartX=-673.316 StartY=-678.872 StartZ=0 EndX=-673.316 EndY=-700.143 EndZ=0
    g1: LineSegment StartX=-673.316 StartY=-700.143 StartZ=0 EndX=-521.684 EndY=-700.143 EndZ=0
    g2: LineSegment StartX=-521.684 StartY=-700.143 StartZ=0 EndX=-521.684 EndY=-678.872 EndZ=0
    g3: LineSegment StartX=-521.684 StartY=-678.872 StartZ=0 EndX=-673.316 EndY=-678.872 EndZ=0
  constraints (10):
    c: Coincident(g0,g1)
    c: Coincident(g1,g2)
    c: Coincident(g2,g3)
    c: Coincident(g3,g0)
    c: Vertical(g0)
    c: Vertical(g2)
    c: Horizontal(g1)
    c: Horizontal(g3)
    c: Coincident(g0,g-4)
    c: Coincident(g1,g-3)
FEATURE [PartDesign::Pad] Pad010
  Direction = (0,-1,2e-16)
  Length = 40
  Length2 = 10
  Placement = pos=(0,0,0) rot=(1,0,0;1.5708rad)
  Profile = -> Sketch016
  ReferenceAxis = -> Sketch016 [N_Axis]
  Refine = true
  Suppressed = false
  Type = 0
FEATURE [Sketcher::SketchObject] Sketch017
  ArcFitTolerance = 1e-06
  AttachmentSupport = -> [Pad010]
  ExternalGeometry = -> [Pad010]
  FullyConstrained = true
  MakeInternals = false
  MapMode = 5
  Placement = pos=(0,-2.261e-13,-678.872) rot=(0,0,1;3.14159rad)
  sketch-geometry (4):
    g0: LineSegment StartX=536.684 StartY=850 StartZ=0 EndX=536.684 EndY=826 EndZ=0
    g1: LineSegment StartX=536.684 StartY=826 StartZ=0 EndX=658.316 EndY=826 EndZ=0
    g2: LineSegment StartX=658.316 StartY=826 StartZ=0 EndX=658.316 EndY=850 EndZ=0
    g3: LineSegment StartX=658.316 StartY=850 StartZ=0 EndX=536.684 EndY=850 EndZ=0
  constraints (12):
    c: Coincident(g0,g1)
    c: Coincident(g1,g2)
    c: Coincident(g2,g3)
    c: Coincident(g3,g0)
    c: Vertical(g0)
    c: Vertical(g2)
    c: Horizontal(g1)
    c: Horizontal(g3)
    c: DistanceY(g2,g-4) = 15
    c: DistanceX(g1,g-4) = 15
    c: DistanceY(g-4,g1) = 1
    c: DistanceX(g-3,g0) = 15
FEATURE [PartDesign::Pocket] Pocket006
  BaseFeature = -> Pad010
  Direction = (0,0,-1)
  Length = 5
  Length2 = 5
  Placement = pos=(0,0,0) rot=(1,0,0;1.5708rad)
  Profile = -> Sketch017
  ReferenceAxis = -> Sketch017 [N_Axis]
  Refine = true
  Suppressed = false
  Type = 1
FEATURE [PartDesign::Fillet] Fillet008
  Base = -> Pocket006 [Edge4,Edge20,Edge21,Edge22]
  BaseFeature = -> Pocket006
  Placement = pos=(0,0,0) rot=(1,0,0;1.5708rad)
  Radius = 15
  Refine = true
  SupportTransform = false
  Suppressed = false
  UseAllEdges = false
FEATURE [PartDesign::Fillet] Fillet009
  Base = -> Fillet008 [Edge8,Edge10,Edge26,Edge20]
  BaseFeature = -> Fillet008
  Placement = pos=(0,0,0) rot=(1,0,0;1.5708rad)
  Radius = 5
  Refine = true
  SupportTransform = false
  Suppressed = false
  UseAllEdges = false
FEATURE [PartDesign::Body] Body005
  AllowCompound = false
  Group = -> [DatumPlane004,CopyPocket005,Sketch016,Pad010,Sketch017,Pocket006,Fillet008,Fillet009]
  Origin = -> Origin010
  Tip = -> Fillet009
FEATURE [PartDesign::ShapeBinder] CopyPocket006
  Placement = pos=(0,0,0) rot=(1,0,0;1.5708rad)
  TraceSupport = false
FEATURE [PartDesign::Plane] DatumPlane005
  AttachmentSupport = -> [CopyPocket006]
  Length = 857.323
  MapMode = 5
  Placement = pos=(0,-825,3.729e-13) rot=(1,0,0;1.5708rad)
  ResizeMode = 0
  Width = 1064.15
FEATURE [Sketcher::SketchObject] Sketch018
  ArcFitTolerance = 1e-06
  AttachmentSupport = -> [CopyPocket006]
  ExternalGeometry = -> [CopyPocket006]
  FullyConstrained = true
  MakeInternals = false
  MapMode = 5
  Placement = pos=(0,-825,3.729e-13) rot=(1,0,0;1.5708rad)
  sketch-geometry (4):
    g0: LineSegment StartX=-673.316 StartY=-858.872 StartZ=0 EndX=-673.316 EndY=-880.143 EndZ=0
    g1: LineSegment StartX=-673.316 StartY=-880.143 StartZ=0 EndX=-521.684 EndY=-880.143 EndZ=0
    g2: LineSegment StartX=-521.684 StartY=-880.143 StartZ=0 EndX=-521.684 EndY=-858.872 EndZ=0
    g3: LineSegment StartX=-521.684 StartY=-858.872 StartZ=0 EndX=-673.316 EndY=-858.872 EndZ=0
  constraints (10):
    c: Coincident(g0,g1)
    c: Coincident(g1,g2)
    c: Coincident(g2,g3)
    c: Coincident(g3,g0)
    c: Vertical(g0)
    c: Vertical(g2)
    c: Horizontal(g1)
    c: Horizontal(g3)
    c: Coincident(g0,g-3)
    c: Coincident(g1,g-4)
FEATURE [PartDesign::Pad] Pad011
  Direction = (0,-1,2e-16)
  Length = 40
  Length2 = 10
  Placement = pos=(0,0,0) rot=(1,0,0;1.5708rad)
  Profile = -> Sketch018
  ReferenceAxis = -> Sketch018 [N_Axis]
  Refine = true
  Suppressed = false
  Type = 0
FEATURE [Sketcher::SketchObject] Sketch019
  ArcFitTolerance = 1e-06
  AttachmentSupport = -> [Pad011]
  ExternalGeometry = -> [Pad011]
  FullyConstrained = true
  MakeInternals = false
  MapMode = 5
  Placement = pos=(0,-2.861e-13,-858.872) rot=(0,0,1;3.14159rad)
  sketch-geometry (4):
    g0: LineSegment StartX=536.684 StartY=850 StartZ=0 EndX=536.684 EndY=826 EndZ=0
    g1: LineSegment StartX=536.684 StartY=826 StartZ=0 EndX=658.316 EndY=826 EndZ=0
    g2: LineSegment StartX=658.316 StartY=826 StartZ=0 EndX=658.316 EndY=850 EndZ=0
    g3: LineSegment StartX=658.316 StartY=850 StartZ=0 EndX=536.684 EndY=850 EndZ=0
  constraints (12):
    c: Coincident(g0,g1)
    c: Coincident(g1,g2)
    c: Coincident(g2,g3)
    c: Coincident(g3,g0)
    c: Vertical(g0)
    c: Vertical(g2)
    c: Horizontal(g1)
    c: Horizontal(g3)
    c: DistanceX(g1,g-4) = 15
    c: DistanceY(g2,g-4) = 15
    c: DistanceX(g-3,g0) = 15
    c: DistanceY(g-4,g1) = 1
FEATURE [PartDesign::Pocket] Pocket007
  BaseFeature = -> Pad011
  Direction = (0,0,-1)
  Length = 1
  Length2 = 5
  Placement = pos=(0,0,0) rot=(1,0,0;1.5708rad)
  Profile = -> Sketch019
  ReferenceAxis = -> Sketch019 [N_Axis]
  Refine = true
  Suppressed = false
  Type = 1
FEATURE [PartDesign::Fillet] Fillet010
  Base = -> Pocket007 [Edge4,Edge20,Edge22,Edge21]
  BaseFeature = -> Pocket007
  Placement = pos=(0,0,0) rot=(1,0,0;1.5708rad)
  Radius = 15
  Refine = true
  SupportTransform = false
  Suppressed = false
  UseAllEdges = false
FEATURE [PartDesign::Fillet] Fillet011
  Base = -> Fillet010 [Edge10,Edge26,Edge8,Edge20]
  BaseFeature = -> Fillet010
  Placement = pos=(0,0,0) rot=(1,0,0;1.5708rad)
  Radius = 5
  Refine = true
  SupportTransform = false
  Suppressed = false
  UseAllEdges = false
FEATURE [PartDesign::Body] Body006
  AllowCompound = false
  Group = -> [DatumPlane005,CopyPocket006,Sketch018,Pad011,Sketch019,Pocket007,Fillet010,Fillet011]
  Origin = -> Origin011
  Tip = -> Fillet011
FEATURE [PartDesign::ShapeBinder] CopyPocket007
  Placement = pos=(0,0,0) rot=(1,0,0;1.5708rad)
  TraceSupport = false
FEATURE [PartDesign::Plane] DatumPlane006
  AttachmentSupport = -> [CopyPocket007]
  Length = 748.322
  MapMode = 5
  Placement = pos=(0,-825,3.729e-13) rot=(1,0,0;1.5708rad)
  ResizeMode = 0
  Width = 171.593
FEATURE [Sketcher::SketchObject] Sketch020
  ArcFitTolerance = 1e-06
  AttachmentSupport = -> [CopyPocket007]
  ExternalGeometry = -> [CopyPocket007]
  FullyConstrained = true
  MakeInternals = false
  MapMode = 5
  Placement = pos=(0,-825,3.729e-13) rot=(1,0,0;1.5708rad)
  sketch-geometry (4):
    g0: LineSegment StartX=515.24 StartY=-68.8715 StartZ=0 EndX=515.24 EndY=-90.1429 EndZ=0
    g1: LineSegment StartX=515.24 StartY=-90.1429 StartZ=0 EndX=666.872 EndY=-90.1429 EndZ=0
    g2: LineSegment StartX=666.872 StartY=-90.1429 StartZ=0 EndX=666.872 EndY=-68.8715 EndZ=0
    g3: LineSegment StartX=666.872 StartY=-68.8715 StartZ=0 EndX=515.24 EndY=-68.8715 EndZ=0
  constraints (10):
    c: Coincident(g0,g1)
    c: Coincident(g1,g2)
    c: Coincident(g2,g3)
    c: Coincident(g3,g0)
    c: Vertical(g0)
    c: Vertical(g2)
    c: Horizontal(g1)
    c: Horizontal(g3)
    c: Coincident(g0,g-3)
    c: Coincident(g1,g-4)
FEATURE [PartDesign::Pad] Pad012
  Direction = (0,-1,2e-16)
  Length = 40
  Length2 = 10
  Placement = pos=(0,0,0) rot=(1,0,0;1.5708rad)
  Profile = -> Sketch020
  ReferenceAxis = -> Sketch020 [N_Axis]
  Refine = true
  Suppressed = false
  Type = 0
FEATURE [Sketcher::SketchObject] Sketch021
  ArcFitTolerance = 1e-06
  AttachmentSupport = -> [Pad012]
  ExternalGeometry = -> [Pad012]
  FullyConstrained = true
  MakeInternals = false
  MapMode = 5
  Placement = pos=(0,-2.29e-14,-68.8715) rot=(0,0,1;3.14159rad)
  sketch-geometry (4):
    g0: LineSegment StartX=-651.872 StartY=850 StartZ=0 EndX=-651.872 EndY=826 EndZ=0
    g1: LineSegment StartX=-651.872 StartY=826 StartZ=0 EndX=-530.24 EndY=826 EndZ=0
    g2: LineSegment StartX=-530.24 StartY=826 StartZ=0 EndX=-530.24 EndY=850 EndZ=0
    g3: LineSegment StartX=-530.24 StartY=850 StartZ=0 EndX=-651.872 EndY=850 EndZ=0
  constraints (12):
    c: Coincident(g0,g1)
    c: Coincident(g1,g2)
    c: Coincident(g2,g3)
    c: Coincident(g3,g0)
    c: Vertical(g0)
    c: Vertical(g2)
    c: Horizontal(g1)
    c: Horizontal(g3)
    c: DistanceX(g2,g-4) = 15
    c: DistanceX(g-3,g0) = 15
    c: DistanceY(g-3,g0) = 1
    c: DistanceY(g2,g-4) = 15
FEATURE [PartDesign::Pocket] Pocket008
  BaseFeature = -> Pad012
  Direction = (0,0,-1)
  Length = 5
  Length2 = 5
  Placement = pos=(0,0,0) rot=(1,0,0;1.5708rad)
  Profile = -> Sketch021
  ReferenceAxis = -> Sketch021 [N_Axis]
  Refine = true
  Suppressed = false
  Type = 1
FEATURE [PartDesign::Fillet] Fillet012
  Base = -> Pocket008 [Edge4,Edge20,Edge21,Edge22]
  BaseFeature = -> Pocket008
  Placement = pos=(0,0,0) rot=(1,0,0;1.5708rad)
  Radius = 15
  Refine = true
  SupportTransform = false
  Suppressed = false
  UseAllEdges = false
FEATURE [PartDesign::Fillet] Fillet013
  Base = -> Fillet012 [Edge10,Edge26,Edge8,Edge20]
  BaseFeature = -> Fillet012
  Placement = pos=(0,0,0) rot=(1,0,0;1.5708rad)
  Radius = 5
  Refine = true
  SupportTransform = false
  Suppressed = false
  UseAllEdges = false
FEATURE [PartDesign::Body] Body007
  AllowCompound = false
  Group = -> [DatumPlane006,CopyPocket007,Sketch020,Pad012,Sketch021,Pocket008,Fillet012,Fillet013]
  Origin = -> Origin012
  Tip = -> Fillet013
FEATURE [PartDesign::ShapeBinder] CopyPocket008
  Placement = pos=(0,0,0) rot=(1,0,0;1.5708rad)
  TraceSupport = false
FEATURE [PartDesign::Plane] DatumPlane007
  AttachmentSupport = -> [CopyPocket008]
  Length = 791.707
  MapMode = 5
  Placement = pos=(0,-825,3.729e-13) rot=(1,0,0;1.5708rad)
  ResizeMode = 0
  Width = 459.977
FEATURE [Sketcher::SketchObject] Sketch022
  ArcFitTolerance = 1e-06
  AttachmentSupport = -> [CopyPocket008]
  ExternalGeometry = -> [CopyPocket008]
  FullyConstrained = true
  MakeInternals = false
  MapMode = 5
  Placement = pos=(0,-825,3.729e-13) rot=(1,0,0;1.5708rad)
  sketch-geometry (4):
    g0: LineSegment StartX=515.24 StartY=-313.872 StartZ=0 EndX=515.24 EndY=-335.143 EndZ=0
    g1: LineSegment StartX=515.24 StartY=-335.143 StartZ=0 EndX=666.872 EndY=-335.143 EndZ=0
    g2: LineSegment StartX=666.872 StartY=-335.143 StartZ=0 EndX=666.872 EndY=-313.872 EndZ=0
    g3: LineSegment StartX=666.872 StartY=-313.872 StartZ=0 EndX=515.24 EndY=-313.872 EndZ=0
  constraints (10):
    c: Coincident(g0,g1)
    c: Coincident(g1,g2)
    c: Coincident(g2,g3)
    c: Coincident(g3,g0)
    c: Vertical(g0)
    c: Vertical(g2)
    c: Horizontal(g1)
    c: Horizontal(g3)
    c: Coincident(g0,g-3)
    c: Coincident(g1,g-4)
FEATURE [PartDesign::Pad] Pad013
  Direction = (0,-1,2e-16)
  Length = 40
  Length2 = 10
  Placement = pos=(0,0,0) rot=(1,0,0;1.5708rad)
  Profile = -> Sketch022
  ReferenceAxis = -> Sketch022 [N_Axis]
  Refine = true
  Suppressed = false
  Type = 0
FEATURE [Sketcher::SketchObject] Sketch023
  ArcFitTolerance = 1e-06
  AttachmentSupport = -> [Pad013]
  ExternalGeometry = -> [Pad013]
  FullyConstrained = true
  MakeInternals = false
  MapMode = 5
  Placement = pos=(0,-1.045e-13,-313.872) rot=(0,0,1;3.14159rad)
  sketch-geometry (4):
    g0: LineSegment StartX=-651.872 StartY=850 StartZ=0 EndX=-651.872 EndY=826 EndZ=0
    g1: LineSegment StartX=-651.872 StartY=826 StartZ=0 EndX=-530.24 EndY=826 EndZ=0
    g2: LineSegment StartX=-530.24 StartY=826 StartZ=0 EndX=-530.24 EndY=850 EndZ=0
    g3: LineSegment StartX=-530.24 StartY=850 StartZ=0 EndX=-651.872 EndY=850 EndZ=0
  constraints (12):
    c: Coincident(g0,g1)
    c: Coincident(g1,g2)
    c: Coincident(g2,g3)
    c: Coincident(g3,g0)
    c: Vertical(g0)
    c: Vertical(g2)
    c: Horizontal(g1)
    c: Horizontal(g3)
    c: DistanceX(g2,g-4) = 15
    c: DistanceY(g2,g-4) = 15
    c: DistanceY(g-4,g1) = 1
    c: DistanceX(g-3,g0) = 15
FEATURE [PartDesign::Pocket] Pocket009
  BaseFeature = -> Pad013
  Direction = (0,0,-1)
  Length = 5
  Length2 = 5
  Placement = pos=(0,0,0) rot=(1,0,0;1.5708rad)
  Profile = -> Sketch023
  ReferenceAxis = -> Sketch023 [N_Axis]
  Refine = true
  Suppressed = false
  Type = 1
FEATURE [PartDesign::Fillet] Fillet014
  Base = -> Pocket009 [Edge4,Edge20,Edge21,Edge22]
  BaseFeature = -> Pocket009
  Placement = pos=(0,0,0) rot=(1,0,0;1.5708rad)
  Radius = 15
  Refine = true
  SupportTransform = false
  Suppressed = false
  UseAllEdges = false
FEATURE [PartDesign::Fillet] Fillet015
  Base = -> Fillet014 [Edge10,Edge26,Edge8,Edge20]
  BaseFeature = -> Fillet014
  Placement = pos=(0,0,0) rot=(1,0,0;1.5708rad)
  Radius = 5
  Refine = true
  SupportTransform = false
  Suppressed = false
  UseAllEdges = false
FEATURE [PartDesign::Body] Body008
  AllowCompound = false
  Group = -> [DatumPlane007,CopyPocket008,Sketch022,Pad013,Sketch023,Pocket009,Fillet014,Fillet015]
  Origin = -> Origin013
  Tip = -> Fillet015
FEATURE [PartDesign::ShapeBinder] CopyPocket009
  Placement = pos=(0,0,0) rot=(1,0,0;1.5708rad)
  TraceSupport = false
FEATURE [PartDesign::Plane] DatumPlane008
  AttachmentSupport = -> [CopyPocket009]
  Length = 814.7
  MapMode = 5
  Placement = pos=(0,-825,3.729e-13) rot=(1,0,0;1.5708rad)
  ResizeMode = 0
  Width = 667.971
FEATURE [Sketcher::SketchObject] Sketch024
  ArcFitTolerance = 1e-06
  AttachmentSupport = -> [CopyPocket009]
  ExternalGeometry = -> [CopyPocket009]
  FullyConstrained = true
  MakeInternals = false
  MapMode = 5
  Placement = pos=(0,-825,3.729e-13) rot=(1,0,0;1.5708rad)
  sketch-geometry (4):
    g0: LineSegment StartX=515.24 StartY=-498.872 StartZ=0 EndX=515.24 EndY=-520.143 EndZ=0
    g1: LineSegment StartX=515.24 StartY=-520.143 StartZ=0 EndX=666.872 EndY=-520.143 EndZ=0
    g2: LineSegment StartX=666.872 StartY=-520.143 StartZ=0 EndX=666.872 EndY=-498.872 EndZ=0
    g3: LineSegment StartX=666.872 StartY=-498.872 StartZ=0 EndX=515.24 EndY=-498.872 EndZ=0
  constraints (10):
    c: Coincident(g0,g1)
    c: Coincident(g1,g2)
    c: Coincident(g2,g3)
    c: Coincident(g3,g0)
    c: Vertical(g0)
    c: Vertical(g2)
    c: Horizontal(g1)
    c: Horizontal(g3)
    c: Coincident(g0,g-3)
    c: Coincident(g1,g-4)
FEATURE [PartDesign::Pad] Pad014
  Direction = (0,-1,2e-16)
  Length = 40
  Length2 = 10
  Placement = pos=(0,0,0) rot=(1,0,0;1.5708rad)
  Profile = -> Sketch024
  ReferenceAxis = -> Sketch024 [N_Axis]
  Refine = true
  Suppressed = false
  Type = 0
FEATURE [Sketcher::SketchObject] Sketch025
  ArcFitTolerance = 1e-06
  AttachmentSupport = -> [Pad014]
  ExternalGeometry = -> [Pad014]
  FullyConstrained = true
  MakeInternals = false
  MapMode = 5
  Placement = pos=(0,-1.662e-13,-498.872) rot=(0,0,1;3.14159rad)
  sketch-geometry (4):
    g0: LineSegment StartX=-651.872 StartY=850 StartZ=0 EndX=-651.872 EndY=826 EndZ=0
    g1: LineSegment StartX=-651.872 StartY=826 StartZ=0 EndX=-530.24 EndY=826 EndZ=0
    g2: LineSegment StartX=-530.24 StartY=826 StartZ=0 EndX=-530.24 EndY=850 EndZ=0
    g3: LineSegment StartX=-530.24 StartY=850 StartZ=0 EndX=-651.872 EndY=850 EndZ=0
  constraints (12):
    c: Coincident(g0,g1)
    c: Coincident(g1,g2)
    c: Coincident(g2,g3)
    c: Coincident(g3,g0)
    c: Vertical(g0)
    c: Vertical(g2)
    c: Horizontal(g1)
    c: Horizontal(g3)
    c: DistanceX(g2,g-4) = 15
    c: DistanceY(g2,g-4) = 15
    c: DistanceY(g-4,g1) = 1
    c: DistanceX(g-3,g0) = 15
FEATURE [PartDesign::Pocket] Pocket010
  BaseFeature = -> Pad014
  Direction = (0,0,-1)
  Length = 5
  Length2 = 5
  Placement = pos=(0,0,0) rot=(1,0,0;1.5708rad)
  Profile = -> Sketch025
  ReferenceAxis = -> Sketch025 [N_Axis]
  Refine = true
  Suppressed = false
  Type = 1
FEATURE [PartDesign::Fillet] Fillet016
  Base = -> Pocket010 [Edge20,Edge4,Edge22,Edge21]
  BaseFeature = -> Pocket010
  Placement = pos=(0,0,0) rot=(1,0,0;1.5708rad)
  Radius = 15
  Refine = true
  SupportTransform = false
  Suppressed = false
  UseAllEdges = false
FEATURE [PartDesign::Fillet] Fillet017
  Base = -> Fillet016 [Edge10,Edge8,Edge26,Edge20]
  BaseFeature = -> Fillet016
  Placement = pos=(0,0,0) rot=(1,0,0;1.5708rad)
  Radius = 5
  Refine = true
  SupportTransform = false
  Suppressed = false
  UseAllEdges = false
FEATURE [PartDesign::Body] Body009
  AllowCompound = false
  Group = -> [DatumPlane008,CopyPocket009,Sketch024,Pad014,Sketch025,Pocket010,Fillet016,Fillet017]
  Origin = -> Origin014
  Tip = -> Fillet017
FEATURE [PartDesign::ShapeBinder] CopyPocket010
  Placement = pos=(0,0,0) rot=(1,0,0;1.5708rad)
  TraceSupport = false
FEATURE [PartDesign::Plane] DatumPlane009
  AttachmentSupport = -> [CopyPocket010]
  Length = 833.535
  MapMode = 5
  Placement = pos=(0,-825,3.729e-13) rot=(1,0,0;1.5708rad)
  ResizeMode = 0
  Width = 866.806
FEATURE [Sketcher::SketchObject] Sketch026
  ArcFitTolerance = 1e-06
  AttachmentSupport = -> [CopyPocket010]
  ExternalGeometry = -> [CopyPocket010]
  FullyConstrained = true
  MakeInternals = false
  MapMode = 5
  Placement = pos=(0,-825,3.729e-13) rot=(1,0,0;1.5708rad)
  sketch-geometry (4):
    g0: LineSegment StartX=515.24 StartY=-678.872 StartZ=0 EndX=515.24 EndY=-700.143 EndZ=0
    g1: LineSegment StartX=515.24 StartY=-700.143 StartZ=0 EndX=666.872 EndY=-700.143 EndZ=0
    g2: LineSegment StartX=666.872 StartY=-700.143 StartZ=0 EndX=666.872 EndY=-678.872 EndZ=0
    g3: LineSegment StartX=666.872 StartY=-678.872 StartZ=0 EndX=515.24 EndY=-678.872 EndZ=0
  constraints (10):
    c: Coincident(g0,g1)
    c: Coincident(g1,g2)
    c: Coincident(g2,g3)
    c: Coincident(g3,g0)
    c: Vertical(g0)
    c: Vertical(g2)
    c: Horizontal(g1)
    c: Horizontal(g3)
    c: Coincident(g0,g-3)
    c: Coincident(g1,g-4)
FEATURE [PartDesign::Pad] Pad015
  Direction = (0,-1,2e-16)
  Length = 40
  Length2 = 10
  Placement = pos=(0,0,0) rot=(1,0,0;1.5708rad)
  Profile = -> Sketch026
  ReferenceAxis = -> Sketch026 [N_Axis]
  Refine = true
  Suppressed = false
  Type = 0
FEATURE [Sketcher::SketchObject] Sketch027
  ArcFitTolerance = 1e-06
  AttachmentSupport = -> [Pad015]
  ExternalGeometry = -> [Pad015]
  FullyConstrained = true
  MakeInternals = false
  MapMode = 5
  Placement = pos=(0,-2.261e-13,-678.872) rot=(0,0,1;3.14159rad)
  sketch-geometry (4):
    g0: LineSegment StartX=-651.872 StartY=850 StartZ=0 EndX=-651.872 EndY=826 EndZ=0
    g1: LineSegment StartX=-651.872 StartY=826 StartZ=0 EndX=-530.24 EndY=826 EndZ=0
    g2: LineSegment StartX=-530.24 StartY=826 StartZ=0 EndX=-530.24 EndY=850 EndZ=0
    g3: LineSegment StartX=-530.24 StartY=850 StartZ=0 EndX=-651.872 EndY=850 EndZ=0
  constraints (12):
    c: Coincident(g0,g1)
    c: Coincident(g1,g2)
    c: Coincident(g2,g3)
    c: Coincident(g3,g0)
    c: Vertical(g0)
    c: Vertical(g2)
    c: Horizontal(g1)
    c: Horizontal(g3)
    c: DistanceX(g-3,g0) = 15
    c: DistanceY(g2,g-4) = 15
    c: DistanceX(g2,g-4) = 15
    c: DistanceY(g-4,g1) = 1
FEATURE [PartDesign::Pocket] Pocket011
  BaseFeature = -> Pad015
  Direction = (0,0,-1)
  Length = 5
  Length2 = 5
  Placement = pos=(0,0,0) rot=(1,0,0;1.5708rad)
  Profile = -> Sketch027
  ReferenceAxis = -> Sketch027 [N_Axis]
  Refine = true
  Suppressed = false
  Type = 1
FEATURE [PartDesign::Fillet] Fillet018
  Base = -> Pocket011 [Edge4,Edge20,Edge21,Edge22]
  BaseFeature = -> Pocket011
  Placement = pos=(0,0,0) rot=(1,0,0;1.5708rad)
  Radius = 15
  Refine = true
  SupportTransform = false
  Suppressed = false
  UseAllEdges = false
FEATURE [PartDesign::Fillet] Fillet019
  Base = -> Fillet018 [Edge10,Edge26,Edge8,Edge20]
  BaseFeature = -> Fillet018
  Placement = pos=(0,0,0) rot=(1,0,0;1.5708rad)
  Radius = 5
  Refine = true
  SupportTransform = false
  Suppressed = false
  UseAllEdges = false
FEATURE [PartDesign::Body] Body010
  AllowCompound = false
  Group = -> [DatumPlane009,CopyPocket010,Sketch026,Pad015,Sketch027,Pocket011,Fillet018,Fillet019]
  Origin = -> Origin015
  Tip = -> Fillet019
FEATURE [PartDesign::ShapeBinder] CopyPocket011
  Placement = pos=(0,0,0) rot=(1,0,0;1.5708rad)
  TraceSupport = false
FEATURE [PartDesign::Plane] DatumPlane010
  AttachmentSupport = -> [CopyPocket011]
  Length = 850.143
  MapMode = 5
  Placement = pos=(0,-825,3.729e-13) rot=(1,0,0;1.5708rad)
  ResizeMode = 0
  Width = 1063.41
FEATURE [Sketcher::SketchObject] Sketch028
  ArcFitTolerance = 1e-06
  AttachmentSupport = -> [CopyPocket011]
  ExternalGeometry = -> [CopyPocket011]
  FullyConstrained = true
  MakeInternals = false
  MapMode = 5
  Placement = pos=(0,-825,3.729e-13) rot=(1,0,0;1.5708rad)
  sketch-geometry (4):
    g0: LineSegment StartX=515.24 StartY=-858.872 StartZ=0 EndX=515.24 EndY=-880.143 EndZ=0
    g1: LineSegment StartX=515.24 StartY=-880.143 StartZ=0 EndX=666.872 EndY=-880.143 EndZ=0
    g2: LineSegment StartX=666.872 StartY=-880.143 StartZ=0 EndX=666.872 EndY=-858.872 EndZ=0
    g3: LineSegment StartX=666.872 StartY=-858.872 StartZ=0 EndX=515.24 EndY=-858.872 EndZ=0
  constraints (10):
    c: Coincident(g0,g1)
    c: Coincident(g1,g2)
    c: Coincident(g2,g3)
    c: Coincident(g3,g0)
    c: Vertical(g0)
    c: Vertical(g2)
    c: Horizontal(g1)
    c: Horizontal(g3)
    c: Coincident(g0,g-3)
    c: Coincident(g1,g-4)
FEATURE [PartDesign::Pad] Pad016
  Direction = (0,-1,2e-16)
  Length = 40
  Length2 = 10
  Placement = pos=(0,0,0) rot=(1,0,0;1.5708rad)
  Profile = -> Sketch028
  ReferenceAxis = -> Sketch028 [N_Axis]
  Refine = true
  Suppressed = false
  Type = 0
FEATURE [Sketcher::SketchObject] Sketch029
  ArcFitTolerance = 1e-06
  AttachmentSupport = -> [Pad016]
  ExternalGeometry = -> [Pad016]
  FullyConstrained = true
  MakeInternals = false
  MapMode = 5
  Placement = pos=(0,-2.861e-13,-858.872) rot=(0,0,1;3.14159rad)
  sketch-geometry (4):
    g0: LineSegment StartX=-651.872 StartY=850 StartZ=0 EndX=-651.872 EndY=826 EndZ=0
    g1: LineSegment StartX=-651.872 StartY=826 StartZ=0 EndX=-530.24 EndY=826 EndZ=0
    g2: LineSegment StartX=-530.24 StartY=826 StartZ=0 EndX=-530.24 EndY=850 EndZ=0
    g3: LineSegment StartX=-530.24 StartY=850 StartZ=0 EndX=-651.872 EndY=850 EndZ=0
  constraints (12):
    c: Coincident(g0,g1)
    c: Coincident(g1,g2)
    c: Coincident(g2,g3)
    c: Coincident(g3,g0)
    c: Vertical(g0)
    c: Vertical(g2)
    c: Horizontal(g1)
    c: Horizontal(g3)
    c: DistanceY(g-4,g1) = 1
    c: DistanceX(g2,g-4) = 15
    c: DistanceY(g2,g-4) = 15
    c: DistanceX(g-3,g0) = 15
FEATURE [PartDesign::Pocket] Pocket012
  BaseFeature = -> Pad016
  Direction = (0,0,-1)
  Length = 5
  Length2 = 5
  Placement = pos=(0,0,0) rot=(1,0,0;1.5708rad)
  Profile = -> Sketch029
  ReferenceAxis = -> Sketch029 [N_Axis]
  Refine = true
  Suppressed = false
  Type = 1
FEATURE [PartDesign::Fillet] Fillet020
  Base = -> Pocket012 [Edge4,Edge20,Edge22,Edge21]
  BaseFeature = -> Pocket012
  Placement = pos=(0,0,0) rot=(1,0,0;1.5708rad)
  Radius = 15
  Refine = true
  SupportTransform = false
  Suppressed = false
  UseAllEdges = false
FEATURE [PartDesign::Fillet] Fillet021
  Base = -> Fillet020 [Edge8,Edge10,Edge26,Edge20]
  BaseFeature = -> Fillet020
  Placement = pos=(0,0,0) rot=(1,0,0;1.5708rad)
  Radius = 5
  Refine = true
  SupportTransform = false
  Suppressed = false
  UseAllEdges = false
FEATURE [PartDesign::Body] Body011
  AllowCompound = false
  Group = -> [DatumPlane010,CopyPocket011,Sketch028,Pad016,Sketch029,Pocket012,Fillet020,Fillet021]
  Origin = -> Origin016
  Tip = -> Fillet021
FEATURE [App::Part] Part001  label="handle_p"
  Group = -> [Body001,Body002,Body003,Body004,Body005,Body006,Body007,Body008,Body009,Body010,Body011]
  Origin = -> Origin006
  Placement = pos=(0,412.5,0) rot=(0,0,1;0rad)
FEATURE [Assembly::JointGroup] Joints001
FEATURE [App::Link] handle_p  label="handle_p001"
  LinkPlacement = pos=(0,412.5,1000) rot=(0,0,1;0rad)
  LinkedObject = -> Part001
  Placement = pos=(0,412.5,1000) rot=(0,0,1;0rad)
FEATURE [Assembly::AssemblyObject] Assembly001  label="handle_a"
  Group = -> [Joints001,handle_p]
  Origin = -> Origin018
  Placement = pos=(0,412.5,1000) rot=(0,0,1;0rad)
  Type = Assembly
FEATURE [Part::FeaturePython] Clone  label="body_clone"  # Draft clone (typed FeaturePython)
  AttacherType = Attacher::AttachEngine3D
  Fuse = false
  Objects = -> [Assembly]
  Scale = (1,1,1)
FEATURE [Part::FeaturePython] Clone001  label="handle_clone"  # Draft clone (typed FeaturePython)
  AttacherType = Attacher::AttachEngine3D
  Fuse = false
  Objects = -> [Assembly001]
  Scale = (1,1,1)
FEATURE [PartDesign::ShapeBinder] CopyPad005
  Placement = pos=(0,-20,9e-15) rot=(0,0,1;0rad)
  TraceSupport = false
FEATURE [PartDesign::Plane] DatumPlane011
  AttachmentSupport = -> [CopyPad005]
  Length = 899.662
  MapMode = 5
  Placement = pos=(0,-95,2.55e-14) rot=(1,0,0;1.5708rad)
  ResizeMode = 0
  Width = 1568.05
FEATURE [Sketcher::SketchObject] Sketch030
  ArcFitTolerance = 1e-06
  AttachmentSupport = -> [CopyPad005]
  ExternalGeometry = -> [CopyPad005]
  FullyConstrained = false
  MakeInternals = false
  MapMode = 5
  Placement = pos=(0,-95,2.55e-14) rot=(1,0,0;1.5708rad)
  sketch-geometry (4):
    g0: LineSegment StartX=-351.618 StartY=995.137 StartZ=0 EndX=-351.618 EndY=0 EndZ=0
    g1: LineSegment StartX=-351.618 StartY=0 StartZ=0 EndX=351.618 EndY=0 EndZ=0
    g2: LineSegment StartX=351.618 StartY=0 StartZ=0 EndX=351.618 EndY=995.137 EndZ=0
    g3: ArcOfCircle CenterX=1.05374e-11 CenterY=995.137 CenterZ=0 NormalX=0 NormalY=0 NormalZ=1 AngleXU=0 Radius=351.618 StartAngle=8.98854e-10 EndAngle=3.14159
  constraints (10):
    c: Coincident(g0,g1)
    c: Coincident(g1,g2)
    c: Vertical(g0)
    c: Vertical(g2)
    c: Horizontal(g1)
    c: Coincident(g0,g-4)
    c: Coincident(g1,g-3)
    c: Coincident(g3,g0)
    c: Coincident(g3,g2)
    c: Tangent(g3,g-5)
FEATURE [PartDesign::Pad] Pad017
  Direction = (0,-1,2e-16)
  Length = 5
  Length2 = 10
  Placement = pos=(0,-20,9e-15) rot=(0,0,1;0rad)
  Profile = -> Sketch030
  ReferenceAxis = -> Sketch030 [N_Axis]
  Refine = true
  Suppressed = false
  Type = 0
FEATURE [PartDesign::Body] Body012
  AllowCompound = false
  Group = -> [DatumPlane011,CopyPad005,Sketch030,Pad017]
  Origin = -> Origin020
  Placement = pos=(0,412.5,0) rot=(0,0,1;0rad)
  Tip = -> Pad017
FEATURE [Assembly::JointGroup] Joints002
FEATURE [App::Link] Body013
  LinkPlacement = pos=(0,412.5,1000) rot=(0,0,1;0rad)
  LinkedObject = -> Body012
  Placement = pos=(0,412.5,1000) rot=(0,0,1;0rad)
FEATURE [Assembly::AssemblyObject] Assembly002  label="glass_a"
  Group = -> [Joints002,Body013]
  Origin = -> Origin021
  Placement = pos=(0,412.5,1000) rot=(0,0,1;0rad)
  Type = Assembly
FEATURE [Part::FeaturePython] Clone002  label="glass_clone"  # Draft clone (typed FeaturePython)
  AttacherType = Attacher::AttachEngine3D
  Fuse = false
  Objects = -> [Assembly002]
  Scale = (1,1,1)
FEATURE [App::Part] Part  label="dressing_table"
  Group = -> [Clone,Clone001,Clone002]
  Origin = -> Origin019
